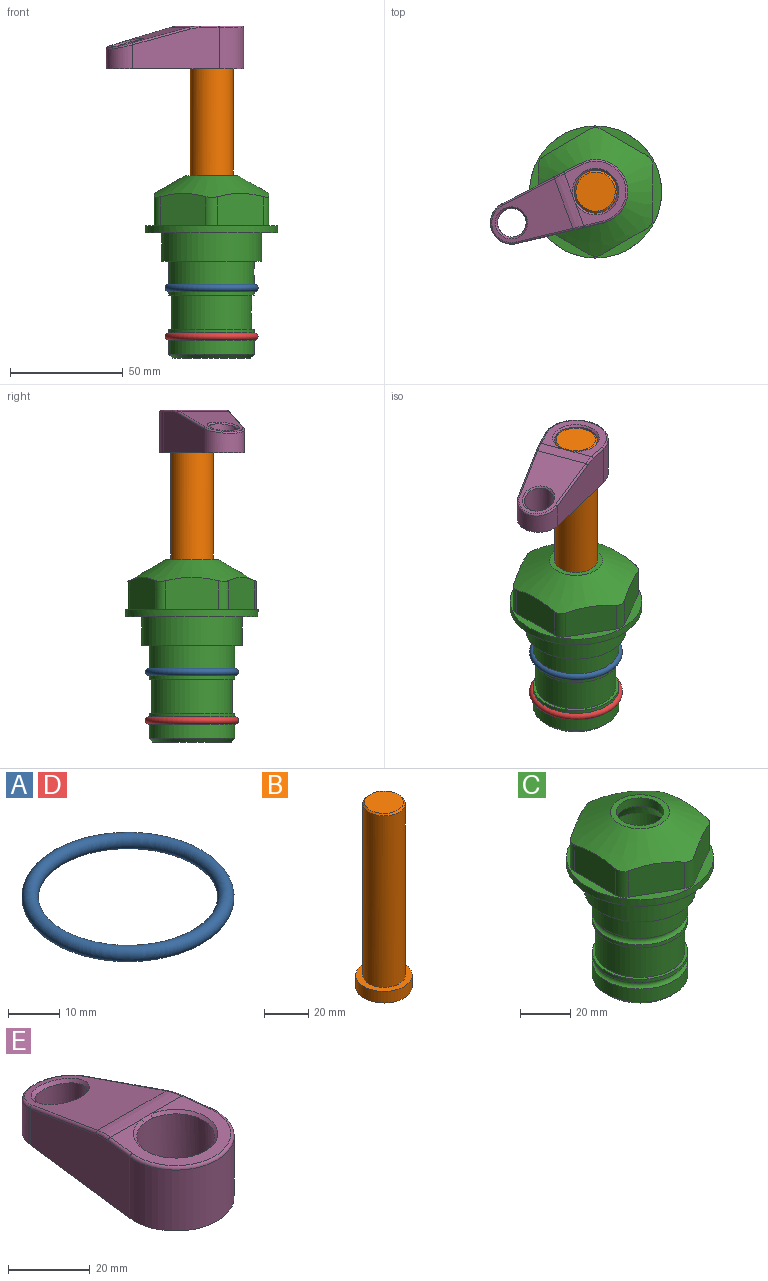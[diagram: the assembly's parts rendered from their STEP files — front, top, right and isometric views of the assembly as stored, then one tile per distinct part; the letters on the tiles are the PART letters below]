
ASSEMBLY  parts=5 mates=4
PART A: 1 faces, bbox 44.7x44.7x3.2 mm
  f0: torus R=19.05mm, axis (0,0,1), area 1193.9mm2
PART B: 6 faces, bbox 25.4x25.4x101.6 mm
  f0: plane 17.46x17.46mm, normal (0,0,1), area 239.5mm2, adj f5
  f1: plane 25.4x25.4mm, normal (0,0,-1), area 506.7mm2, adj f2
  f2: cylinder r=12.7mm len=25.4mm, axis (0,0,1), area 506.7mm2, adj f1,f3
  f3: plane 25.4x25.4mm, normal (0,0,1), area 221.7mm2, adj f2,f4
  f4: cylinder r=9.53mm len=94.46mm, axis (0,0,1), area 5653mm2, adj f3,f5
  f5: cone r=8.73mm half-angle=45deg, axis (0,0,-1), area 64.4mm2, adj f0,f4
PART C: 36 faces, bbox 58.7x58.7x81 mm
  f0: cylinder r=17.78mm len=35.56mm, axis (0,0,1), area 1670.8mm2, adj f23,f24,f31
  f1: cylinder r=19.05mm len=38.1mm, axis (0,0,1), area 1191.9mm2, adj f26,f27,f30
  f2: plane 58.66x58.66mm, normal (0,0,-1), area 1150.6mm2, adj f3,f28
  f3: cylinder r=29.33mm len=58.66mm, axis (0,0,-1), area 585.1mm2, adj f2,f4
  f4: plane 58.66x58.66mm, normal (0,0,1), area 475.9mm2, adj f3,f5,f6,f7,f8,f9,f10,f11
  f5: plane 20.32x14.34mm, normal (-0.5,0.87,0), area 324.4mm2, adj f4,f15,f16,f17
  f6: plane 20.32x14.34mm, normal (0.5,0.87,0), area 324.4mm2, adj f4,f14,f15,f17
  f7: plane 23.48x14.34mm, normal (1,0,0), area 324.4mm2, adj f4,f13,f14,f17
  f8: plane 20.32x14.34mm, normal (0.5,-0.87,0), area 324.4mm2, adj f4,f12,f13,f17
  f9: plane 20.32x14.34mm, normal (-0.5,-0.87,0), area 324.4mm2, adj f4,f11,f12,f17
  f10: plane 23.48x14.34mm, normal (-1,0,0), area 324.4mm2, adj f4,f11,f16,f17
  f11: cylinder r=5.08mm len=12.85mm, axis (0,0,-1), area 67.2mm2, adj f4,f9,f10,f17
  f12: cylinder r=5.08mm len=12.85mm, axis (0,0,-1), area 67.2mm2, adj f4,f8,f9,f17
  f13: cylinder r=5.08mm len=12.85mm, axis (0,0,-1), area 67.2mm2, adj f4,f7,f8,f17
  f14: cylinder r=5.08mm len=12.85mm, axis (0,0,-1), area 67.2mm2, adj f4,f6,f7,f17
  f15: cylinder r=5.08mm len=12.85mm, axis (0,0,-1), area 67.2mm2, adj f4,f5,f6,f17
  f16: cylinder r=5.08mm len=12.85mm, axis (0,0,-1), area 67.2mm2, adj f4,f5,f10,f17
  f17: cone r=11.73mm half-angle=60deg, axis (0,0,-1), area 2071.8mm2, adj f5,f6,f7,f8,f9,f10,f11,f12
  f18: plane 23.46x23.46mm, normal (0,0,1), area 147.4mm2, adj f17,f35
  f19: plane 34.93x34.93mm, normal (0,0,-1), area 958mm2, adj f29
  f20: cylinder r=19.05mm len=38.1mm, axis (0,0,1), area 760.1mm2, adj f21,f29
  f21: torus R=19.05mm, axis (0,0,1), area 565.3mm2, adj f20,f22
  f22: cylinder r=19.05mm len=38.1mm, axis (0,0,1), area 190mm2, adj f21,f23
  f23: plane 38.1x38.1mm, normal (0,0,1), area 146.9mm2, adj f0,f22
  f24: plane 38.1x38.1mm, normal (0,0,-1), area 146.9mm2, adj f0,f25
  f25: cylinder r=19.05mm len=38.1mm, axis (0,0,1), area 190mm2, adj f24,f26
  f26: torus R=19.05mm, axis (0,0,1), area 565.3mm2, adj f1,f25
  f27: plane 44.45x44.45mm, normal (0,0,-1), area 411.7mm2, adj f1,f28
  f28: cylinder r=22.23mm len=44.45mm, axis (0,0,1), area 1773.5mm2, adj f2,f27
  f29: cone r=19.05mm half-angle=45deg, axis (0,0,1), area 257.5mm2, adj f19,f20
  f30: cylinder r=3.17mm len=6.75mm, axis (-1,0,0), area 128mm2, adj f1,f33
  f31: cylinder r=3.17mm len=6.35mm, axis (-1,0,0), area 102.5mm2, adj f0,f33
  f32: plane 25.4x25.4mm, normal (0,0,1), area 506.7mm2, adj f33
  f33: cylinder r=12.7mm len=66.42mm, axis (0,0,-1), area 5236.2mm2, adj f30,f31,f32,f34
  f34: cone r=9.53mm half-angle=30deg, axis (0,0,-1), area 443.4mm2, adj f33,f35
  f35: cylinder r=9.53mm len=19.05mm, axis (0,0,-1), area 240.9mm2, adj f18,f34
PART D: same geometry as A
PART E: 31 faces, bbox 31.7x65.5x19.8 mm
  f0: plane 39.12x18.26mm, normal (0.99,0.12,0), area 612.2mm2, adj f1,f4,f7,f11,f13,f15
  f1: cylinder r=9.53mm len=18.91mm, axis (0,0,-1), area 296.1mm2, adj f0,f2,f7,f17
  f2: plane 39.12x18.26mm, normal (-0.99,0.12,0), area 612.2mm2, adj f1,f4,f7,f12,f14,f16
  f3: cylinder r=6.35mm len=12.7mm, axis (0,0,-1), area 362.4mm2, adj f7,f18
  f4: cylinder r=14.29mm len=28.58mm, axis (0,0,-1), area 882.2mm2, adj f0,f2,f7,f10
  f5: cylinder r=9.53mm len=19.05mm, axis (0,0,-1), area 1092.6mm2, adj f7,f19,f20
  f6: plane 26.99x23.69mm, normal (0,0,1), area 216.2mm2, adj f9,f10,f11,f12,f19
  f7: plane 63.5x28.58mm, normal (0,0,-1), area 661.8mm2, adj f0,f1,f2,f3,f4,f5,f22,f23
  f8: plane 33.52x23.6mm, normal (0,0.26,0.97), area 486mm2, adj f9,f15,f16,f17,f18
  f9: cylinder r=19.05mm len=24.72mm, axis (1,0,0), area 120.4mm2, adj f6,f8,f13,f14,f20
  f10: torus R=13.49mm, axis (0,0,1), area 59mm2, adj f4,f6,f11,f12
  f11: cylinder r=0.79mm len=8.67mm, axis (0.12,-0.99,0), area 10.8mm2, adj f0,f6,f10,f13
  f12: cylinder r=0.79mm len=8.67mm, axis (0.12,0.99,0), area 10.8mm2, adj f2,f6,f10,f14
  f13: bspline ~4.95x1.42mm, area 6.1mm2, adj f0,f9,f11,f15
  f14: bspline ~4.95x1.42mm, area 6.1mm2, adj f2,f9,f12,f16
  f15: cylinder r=0.79mm len=25.95mm, axis (0.12,-0.96,0.26), area 32.9mm2, adj f0,f8,f13,f17
  f16: cylinder r=0.79mm len=25.95mm, axis (0.12,0.96,-0.26), area 32.9mm2, adj f2,f8,f14,f17
  f17: bspline ~18.91x8.38mm, area 30mm2, adj f1,f8,f15,f16
  f18: bspline ~14.29x14.29mm, area 48.3mm2, adj f3,f8
  f19: cone r=9.53mm half-angle=45deg, axis (0,0,1), area 66.5mm2, adj f5,f6,f20
  f20: bspline ~3.22x0.96mm, area 3.5mm2, adj f5,f9,f19
  f21: plane 2.75x2.72mm, normal (0,0,-1), area 2.9mm2, adj f23,f25,f28
  f22: plane 23.05x15.88mm, normal (-0.99,-0.12,0), area 323.6mm2, adj f7,f25,f26,f27,f28,f29
  f23: plane 23.05x15.88mm, normal (0.99,-0.12,0), area 323.6mm2, adj f7,f21,f25,f27,f28,f30
  f24: cylinder r=9.53mm len=10.69mm, axis (0,0,-1), area 114.7mm2, adj f7,f27,f29,f30
  f25: cylinder r=12.7mm len=20.59mm, axis (0,0,-1), area 381.1mm2, adj f7,f21,f22,f23,f26,f28
  f26: plane 2.75x2.72mm, normal (0,0,-1), area 2.9mm2, adj f22,f25,f28
  f27: plane 19.72x18.37mm, normal (0,-0.26,-0.97), area 291.8mm2, adj f22,f23,f24,f28,f29,f30
  f28: cylinder r=15.88mm len=19.92mm, axis (1,0,0), area 54.8mm2, adj f21,f22,f23,f25,f26,f27
  f29: cylinder r=1.59mm len=11mm, axis (0,0,-1), area 34.7mm2, adj f7,f22,f24,f27
  f30: cylinder r=1.59mm len=11mm, axis (0,0,-1), area 34.7mm2, adj f7,f23,f24,f27
PLACE A at identity
PLACE B rot(axis=(0,0,1),110.4deg) t=(0,0,27.55)mm
PLACE C at identity fixed
PLACE D t=(0,0,-21.59)mm
PLACE E rot(axis=(0,0,1),110.4deg) t=(0,0,28.35)mm
MATE fastened D.f0 <-> C.f0  axis (0,0,1) through (0,0,-46.1)mm
MATE fastened B.f2 <-> E.f4  axis (0,0,1) through (0,0,91.05)mm
MATE fastened A.f0 <-> C.f0  axis (0,0,1) through (0,0,-24.51)mm
MATE cylindrical B.f2 <-> C.f0  axis (0,0,-1) through (0,0,-10.55)mm
